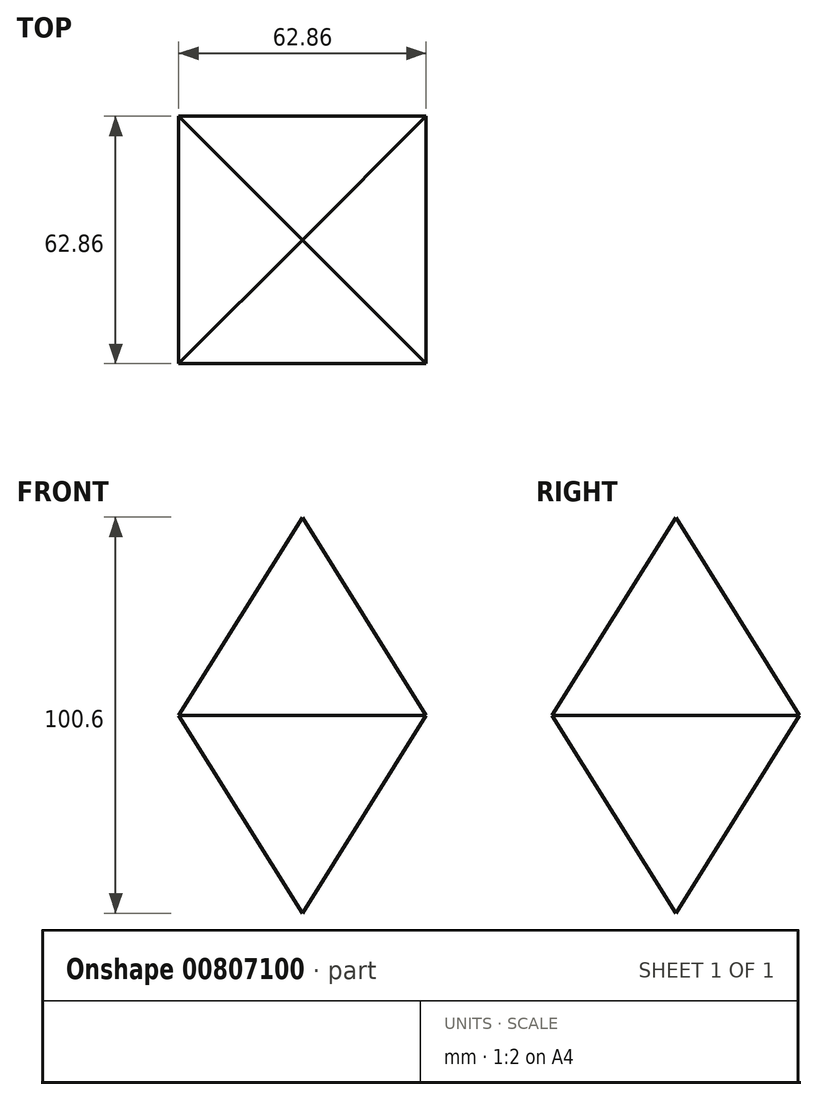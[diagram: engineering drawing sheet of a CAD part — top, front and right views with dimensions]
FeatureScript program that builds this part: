
annotation { "Feature Type Name" : "Feature", "Feature Type Description" : "" }
export const myFeature = defineFeature(function(context is Context, id is Id, definition is map)
    precondition{}
    {
        {
            var Q0;
            Q0=qCreatedBy(makeId("Top.planeOp"),FACE);
            var sketch = newSketch(context, id + "F0", { "sketchPlane" : qUnion([Q0])});
            skLineSegment(sketch, "E0.bottom", {"start": v(31.43, 31.43) * mm, "end": v(-31.43, 31.43) * mm});
            skLineSegment(sketch, "E0.top", {"start": v(31.43, -31.43) * mm, "end": v(-31.43, -31.43) * mm});
            skLineSegment(sketch, "E0.left", {"start": v(31.43, 31.43) * mm, "end": v(31.43, -31.43) * mm});
            skLineSegment(sketch, "E0.right", {"start": v(-31.43, 31.43) * mm, "end": v(-31.43, -31.43) * mm});
            skPoint(sketch, "E0.middle", {"position": v(0, 0) * mm});
            skSolve(sketch);
        }
        {
            var Q0;
            Q0=makeQuery(id+"F0.imprint","IMPRINT",FACE,{"disambiguationData":[TD([[makeQuery(id+"F0.imprint","IMPRINT",EDGE,{"derivedFrom":sQuery(id+"F0.wireOp",EDGE,"E0.bottom")}),1.0]])]});
            extrude(context, id + "F1", {"entities" : qUnion([Q0]), "depth" : 100.33 * mm, "offsetDistance" : 25.4 * mm, "hasDraft" : true, "draftAngle" : 32 * degree, "draftPullDirection" : true, "hasSecondDirection" : true, "secondDirectionOppositeDirection" : true, "secondDirectionDepth" : 61.98 * mm, "hasSecondDirectionDraft" : true, "secondDirectionDraftAngle" : 32 * degree, "secondDirectionDraftPullDirection" : true});
        }
    });
